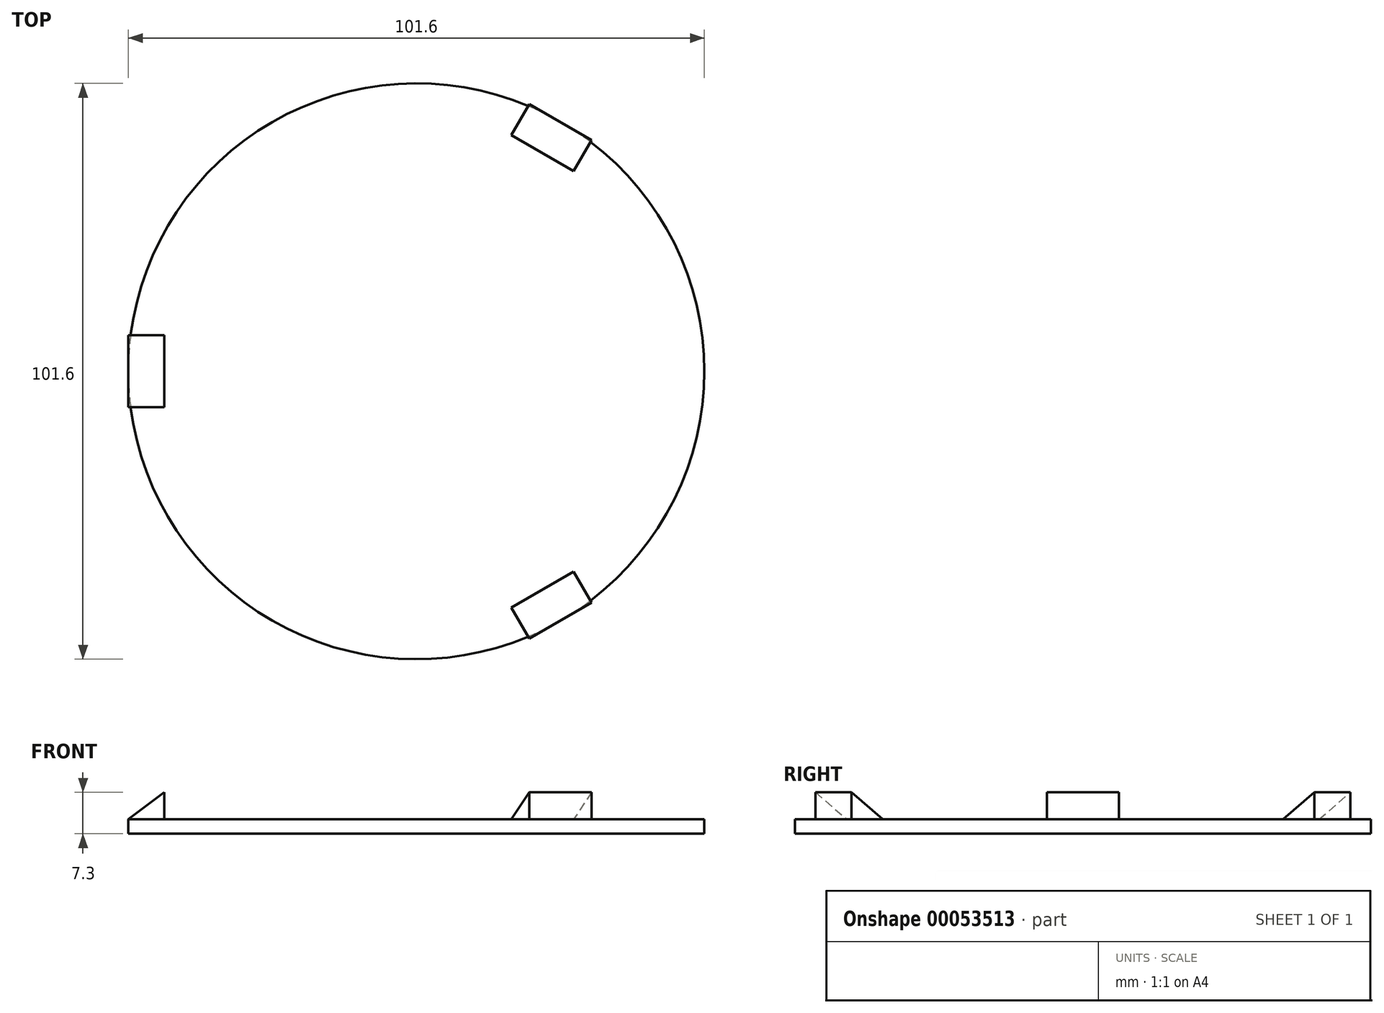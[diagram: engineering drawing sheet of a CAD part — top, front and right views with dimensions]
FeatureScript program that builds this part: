
annotation { "Feature Type Name" : "Feature", "Feature Type Description" : "" }
export const myFeature = defineFeature(function(context is Context, id is Id, definition is map)
    precondition{}
    {
        {
            var Q0;
            Q0=qCreatedBy(makeId("Top.planeOp"),FACE);
            var sketch = newSketch(context, id + "F0", { "sketchPlane" : qUnion([Q0])});
            skCircle(sketch, "E0", {"center": v(0, 0) * mm, "radius": 50.8 * mm});
            skSolve(sketch);
        }
        {
            var Q0;
            Q0 = qSketchRegion(id + "F0", true);
            var Q1;
            Q1=makeQuery(id+"F0.imprint","IMPRINT",FACE,{"disambiguationData":[TD([[makeQuery(id+"F0.imprint","IMPRINT",EDGE,{"derivedFrom":sQuery(id+"F0.wireOp",EDGE,"E0")}),1.0]])]});
            extrude(context, id + "F1", {"entities" : qUnion([Q0, Q1]), "depth" : 2.54 * mm});
        }
        {
            var Q0;
            Q0=makeQuery(id+"F1.opExtrude","CAP_FACE",FACE,{"disambiguationData":[OSD([sQuery(id+"F0.wireOp",EDGE,"E0")])],"isStart":false});
            var sketch = newSketch(context, id + "F2", { "sketchPlane" : qUnion([Q0])});
            skLineSegment(sketch, "E1", {"start": v(-50.8, 0) * mm, "end": v(-50.8, -6.35) * mm});
            skLineSegment(sketch, "E2", {"start": v(-50.8, 0) * mm, "end": v(-50.8, 6.35) * mm});
            skLineSegment(sketch, "E3.bottom", {"start": v(-50.8, 6.35) * mm, "end": v(-44.45, 6.35) * mm});
            skLineSegment(sketch, "E3.top", {"start": v(-50.8, -6.35) * mm, "end": v(-44.45, -6.35) * mm});
            skLineSegment(sketch, "E3.left", {"start": v(-50.8, 6.35) * mm, "end": v(-50.8, -6.35) * mm});
            skLineSegment(sketch, "E3.right", {"start": v(-44.45, 6.35) * mm, "end": v(-44.45, -6.35) * mm});
            skLineSegment(sketch, "E4.1.0", {"start": v(19.9, -47.17) * mm, "end": v(16.73, -41.67) * mm});
            skLineSegment(sketch, "E4.1.1", {"start": v(16.73, -41.67) * mm, "end": v(27.72, -35.32) * mm});
            skLineSegment(sketch, "E4.1.2", {"start": v(19.9, -47.17) * mm, "end": v(30.9, -40.82) * mm});
            skLineSegment(sketch, "E4.1.3", {"start": v(30.9, -40.82) * mm, "end": v(27.72, -35.32) * mm});
            skLineSegment(sketch, "E4.2.0", {"start": v(30.9, 40.82) * mm, "end": v(27.72, 35.32) * mm});
            skLineSegment(sketch, "E4.2.1", {"start": v(27.72, 35.32) * mm, "end": v(16.73, 41.67) * mm});
            skLineSegment(sketch, "E4.2.2", {"start": v(30.9, 40.82) * mm, "end": v(19.9, 47.17) * mm});
            skLineSegment(sketch, "E4.2.3", {"start": v(19.9, 47.17) * mm, "end": v(16.73, 41.67) * mm});
            skPoint(sketch, "E4.center", {"position": v(0, 0) * mm});
            skSolve(sketch);
        }
        {
            var Q0;
            Q0 = qSketchRegion(id + "F2", true);
            extrude(context, id + "F3", {"entities" : qUnion([Q0]), "operationType" : NewBodyOperationType.ADD, "depth" : 12.7 * mm});
        }
        {
            var Q0;
            Q0=makeQuery(id+"F3.opExtrude","SWEPT_FACE",FACE,{"disambiguationData":[OSD([sQuery(id+"F2.wireOp",EDGE,"E3.top")])]});
            var sketch = newSketch(context, id + "F4", { "sketchPlane" : qUnion([Q0])});
            skLineSegment(sketch, "E5", {"start": v(-50.8, 2.54) * mm, "end": v(-44.45, 2.54) * mm});
            skLineSegment(sketch, "E6", {"start": v(-50.8, 2.54) * mm, "end": v(-46.24, 5.96) * mm});
            skLineSegment(sketch, "E7", {"start": v(-46.24, 5.96) * mm, "end": v(-44.45, 7.3) * mm});
            skLineSegment(sketch, "E8", {"start": v(-44.45, 7.3) * mm, "end": v(-44.45, 2.54) * mm});
            skSolve(sketch);
        }
        {
            var Q0;
            Q0=makeQuery(id+"F4.imprint","IMPRINT",FACE,{"disambiguationData":[TD([[makeQuery(id+"F4.imprint","IMPRINT",EDGE,{"derivedFrom":sQuery(id+"F4.wireOp",EDGE,"E6")}),1.0]])]});
            extrude(context, id + "F5", {"entities" : qUnion([Q0]), "operationType" : NewBodyOperationType.REMOVE, "oppositeDirection" : true, "depth" : 25.4 * mm});
        }
        {
            var Q0;
            Q0=makeQuery(id+"F3.opExtrude","SWEPT_FACE",FACE,{"disambiguationData":[OSD([sQuery(id+"F2.wireOp",EDGE,"E4.1.3")])]});
            var sketch = newSketch(context, id + "F6", { "sketchPlane" : qUnion([Q0])});
            skLineSegment(sketch, "E9", {"start": v(-44.45, 2.54) * mm, "end": v(-50.8, 2.54) * mm});
            skLineSegment(sketch, "E10", {"start": v(-44.45, 2.54) * mm, "end": v(-50.03, 6.73) * mm});
            skLineSegment(sketch, "E11", {"start": v(-50.03, 6.73) * mm, "end": v(-50.8, 7.3) * mm});
            skSolve(sketch);
        }
        {
            var Q0;
            Q0=makeQuery(id+"F6.imprint","IMPRINT",FACE,{"disambiguationData":[TD([[makeQuery(id+"F6.imprint","IMPRINT",EDGE,{"derivedFrom":sQuery(id+"F6.wireOp",EDGE,"a564e150-08b3-4e87-9317-8c15af26d10a")}),1.0]])]});
            var Q1;
            Q1=makeQuery(id+"F6.imprint","IMPRINT",FACE,{"disambiguationData":[TD([[makeQuery(id+"F6.imprint","IMPRINT",EDGE,{"derivedFrom":sQuery(id+"F6.wireOp",EDGE,"E10")}),-1.0]])]});
            extrude(context, id + "F7", {"entities" : qUnion([Q0, Q1]), "operationType" : NewBodyOperationType.REMOVE, "oppositeDirection" : true, "depth" : 25.4 * mm});
        }
        {
            var Q0;
            Q0=makeQuery(id+"F3.opExtrude","SWEPT_FACE",FACE,{"disambiguationData":[OSD([sQuery(id+"F2.wireOp",EDGE,"E4.2.3")])]});
            var sketch = newSketch(context, id + "F8", { "sketchPlane" : qUnion([Q0])});
            skLineSegment(sketch, "E12", {"start": v(-50.8, 2.54) * mm, "end": v(-44.45, 2.54) * mm});
            skLineSegment(sketch, "E13", {"start": v(-44.45, 2.54) * mm, "end": v(-49.8, 6.56) * mm});
            skLineSegment(sketch, "E14", {"start": v(-49.8, 6.56) * mm, "end": v(-50.8, 7.3) * mm});
            skSolve(sketch);
        }
        {
            var Q0;
            Q0 = qSketchRegion(id + "F8", true);
            var Q1;
            Q1=makeQuery(id+"F8.imprint","IMPRINT",FACE,{"disambiguationData":[TD([[makeQuery(id+"F8.imprint","IMPRINT",EDGE,{"derivedFrom":sQuery(id+"F8.wireOp",EDGE,"E13")}),-1.0]])]});
            extrude(context, id + "F9", {"entities" : qUnion([Q0, Q1]), "operationType" : NewBodyOperationType.REMOVE, "oppositeDirection" : true, "depth" : 25.4 * mm});
        }
    });
